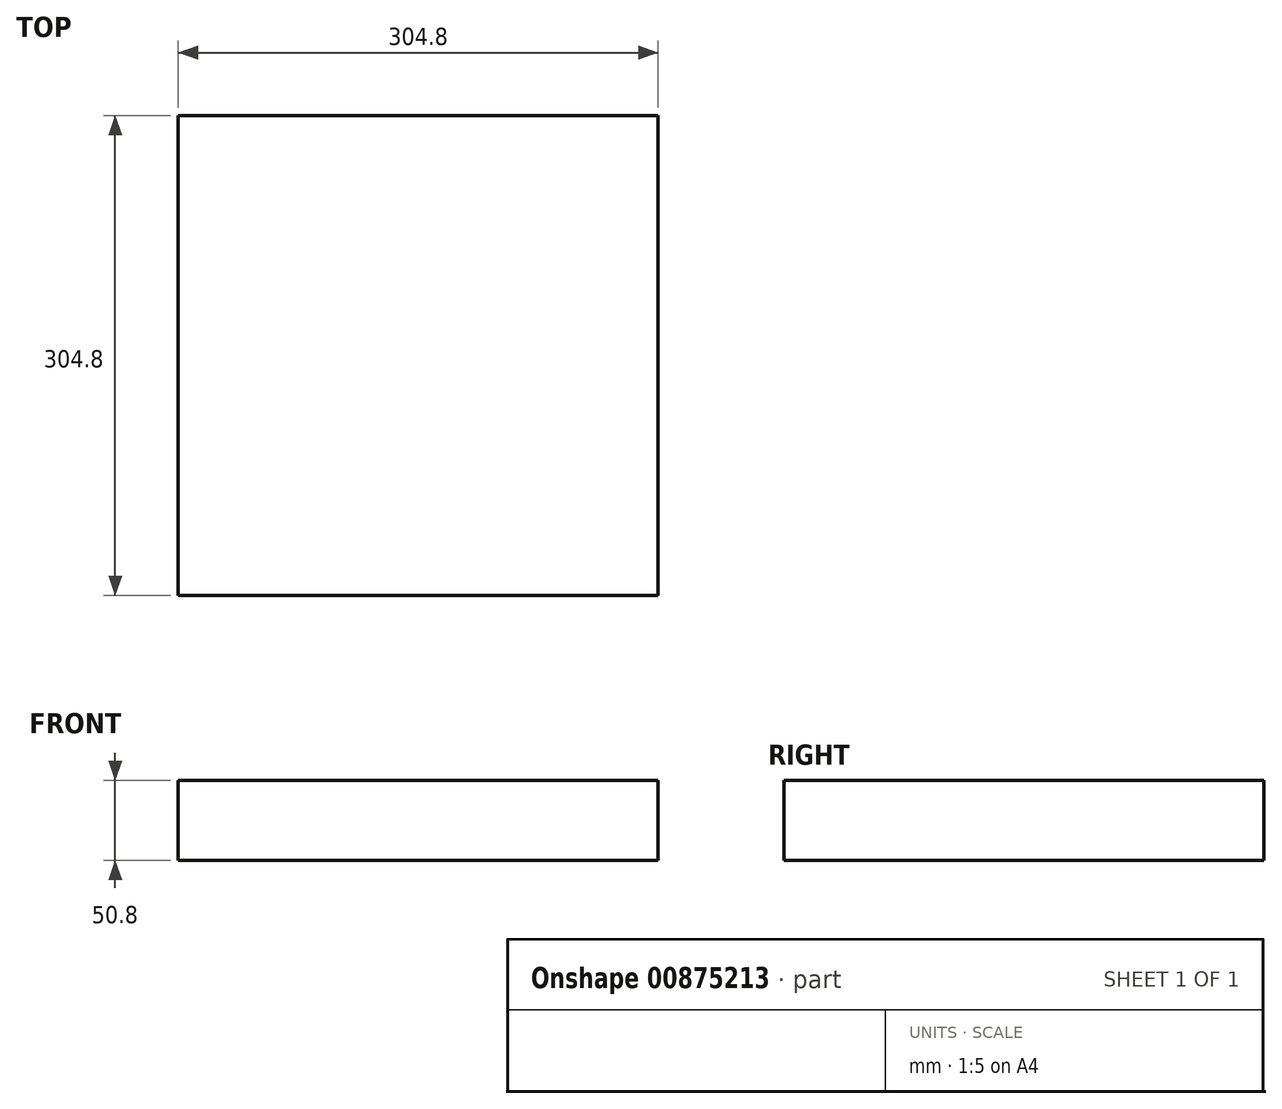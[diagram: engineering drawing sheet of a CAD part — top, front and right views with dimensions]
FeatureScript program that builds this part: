
annotation { "Feature Type Name" : "Feature", "Feature Type Description" : "" }
export const myFeature = defineFeature(function(context is Context, id is Id, definition is map)
    precondition{}
    {
        {
            var Q0;
            Q0=qCreatedBy(makeId("Top.planeOp"),FACE);
            var sketch = newSketch(context, id + "F0", { "sketchPlane" : qUnion([Q0])});
            skLineSegment(sketch, "E0.bottom", {"start": v(-152.4, 152.4) * mm, "end": v(152.4, 152.4) * mm});
            skLineSegment(sketch, "E0.top", {"start": v(-152.4, -152.4) * mm, "end": v(152.4, -152.4) * mm});
            skLineSegment(sketch, "E0.left", {"start": v(-152.4, 152.4) * mm, "end": v(-152.4, -152.4) * mm});
            skLineSegment(sketch, "E0.right", {"start": v(152.4, 152.4) * mm, "end": v(152.4, -152.4) * mm});
            skPoint(sketch, "E0.middle", {"position": v(0, 0) * mm});
            skSolve(sketch);
        }
        {
            var Q0;
            Q0=makeQuery(id+"F0.imprint","IMPRINT",FACE,{"disambiguationData":[TD([[makeQuery(id+"F0.imprint","IMPRINT",EDGE,{"derivedFrom":sQuery(id+"F0.wireOp",EDGE,"E0.bottom")}),-1.0]])]});
            extrude(context, id + "F1", {"entities" : qUnion([Q0]), "depth" : 50.8 * mm, "offsetDistance" : 25.4 * mm});
        }
    });
